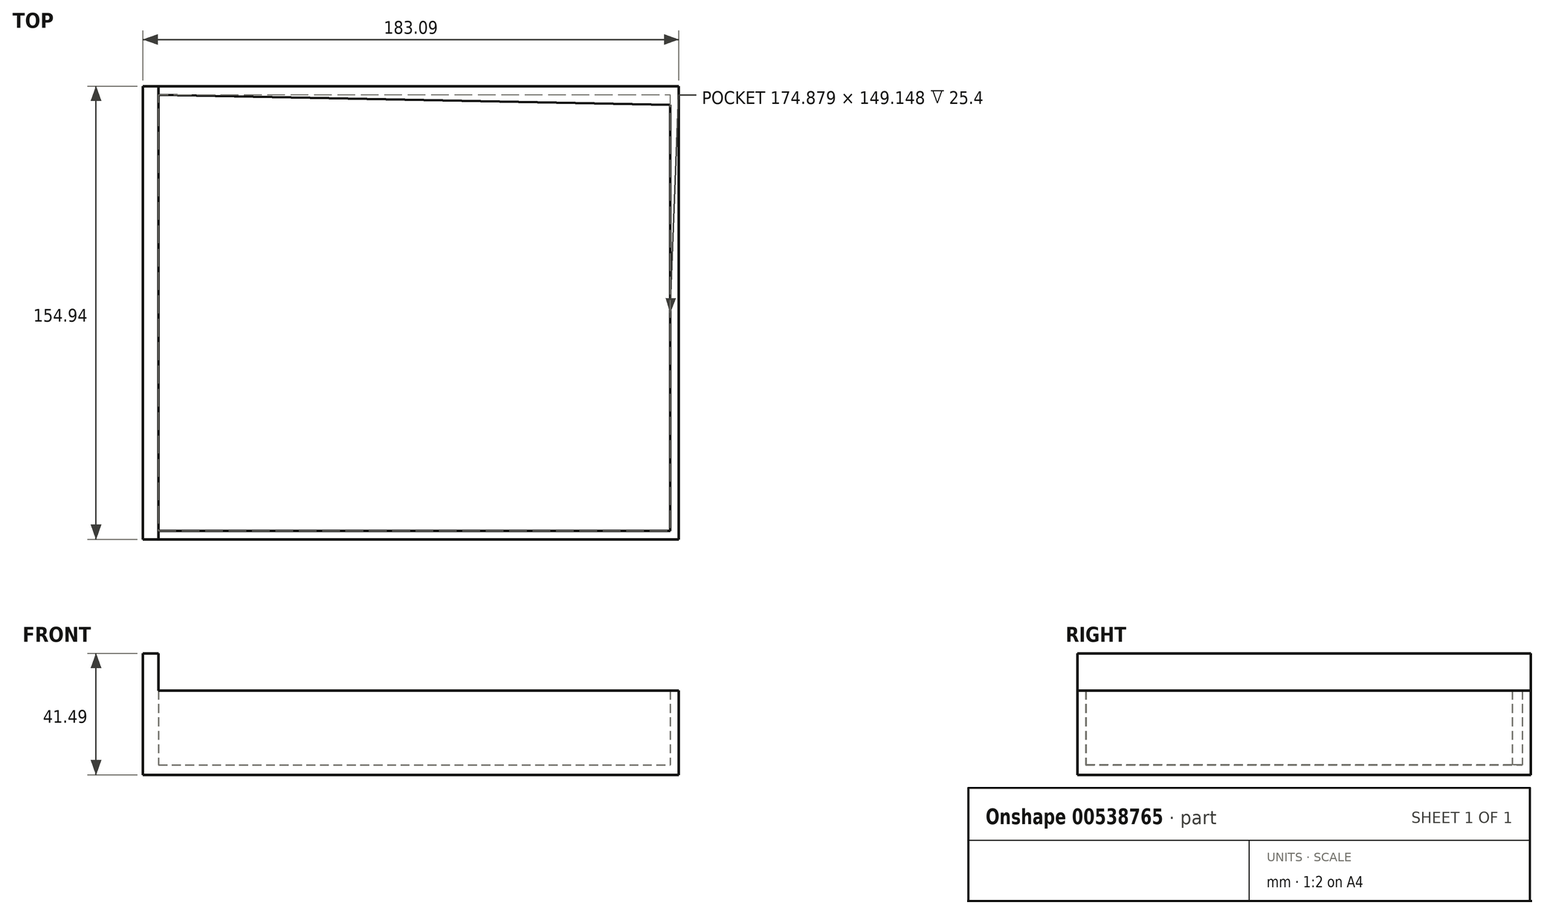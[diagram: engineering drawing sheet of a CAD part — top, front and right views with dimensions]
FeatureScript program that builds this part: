
annotation { "Feature Type Name" : "Feature", "Feature Type Description" : "" }
export const myFeature = defineFeature(function(context is Context, id is Id, definition is map)
    precondition{}
    {
        {
            var Q0;
            Q0=qCreatedBy(makeId("Front.planeOp"),FACE);
            var sketch = newSketch(context, id + "F0", { "sketchPlane" : qUnion([Q0])});
            skLineSegment(sketch, "E0.top", {"start": v(0, 38.1) * mm, "end": v(-5.29, 38.1) * mm});
            skLineSegment(sketch, "E0.left", {"start": v(0, 0) * mm, "end": v(0, 38.1) * mm});
            skLineSegment(sketch, "E1", {"start": v(0, 0) * mm, "end": v(177.8, 0) * mm});
            skLineSegment(sketch, "E2", {"start": v(177.8, 0) * mm, "end": v(177.8, -3.39) * mm});
            skLineSegment(sketch, "E3", {"start": v(177.8, -3.39) * mm, "end": v(-5.29, -3.39) * mm});
            skLineSegment(sketch, "E4", {"start": v(-5.29, 38.1) * mm, "end": v(-5.29, -3.39) * mm});
            skSolve(sketch);
        }
        {
            var Q0;
            Q0 = qSketchRegion(id + "F0", true);
            extrude(context, id + "F1", {"entities" : qUnion([Q0]), "endBound" : BoundingType.SYMMETRIC, "depth" : 154.94 * mm, "offsetDistance" : 25.4 * mm});
        }
        {
            var Q0;
            Q0=makeQuery(id+"F1.opExtrude","SWEPT_FACE",FACE,{"disambiguationData":[OSD([sQuery(id+"F0.wireOp",EDGE,"E0.left")])]});
            var sketch = newSketch(context, id + "F2", { "sketchPlane" : qUnion([Q0])});
            skLineSegment(sketch, "E5.bottom", {"start": v(-64.77, 55.88) * mm, "end": v(64.77, 55.88) * mm});
            skLineSegment(sketch, "E5.top", {"start": v(-64.77, 0) * mm, "end": v(64.77, 0) * mm});
            skLineSegment(sketch, "E5.left", {"start": v(-64.77, 55.88) * mm, "end": v(-64.77, 0) * mm});
            skLineSegment(sketch, "E5.right", {"start": v(64.77, 55.88) * mm, "end": v(64.77, 0) * mm});
            skSolve(sketch);
        }
        {
            var Q0;
            Q0=makeQuery(id+"FWv1kH76DlVqDbQ_1.boolean.opBoolean","MERGE",FACE,{"derivedFrom":[makeQuery(id+"F1.opExtrude","SWEPT_FACE",FACE,{"disambiguationData":[OSD([sQuery(id+"F0.wireOp",EDGE,"E1")])]}),makeQuery(id+"FWv1kH76DlVqDbQ_1.opExtrude","SWEPT_FACE",FACE,{"disambiguationData":[OSD([sQuery(id+"F2.wireOp",EDGE,"E5.top")])]})]});
            var sketch = newSketch(context, id + "F3", { "sketchPlane" : qUnion([Q0])});
            skLineSegment(sketch, "E6", {"start": v(0, -77.47) * mm, "end": v(177.8, -77.47) * mm});
            skLineSegment(sketch, "E7", {"start": v(177.8, -77.47) * mm, "end": v(177.8, 77.47) * mm});
            skLineSegment(sketch, "E8", {"start": v(177.8, 77.47) * mm, "end": v(0, 77.47) * mm});
            skLineSegment(sketch, "E9", {"start": v(0, 77.47) * mm, "end": v(-0.06, 74.55) * mm});
            skLineSegment(sketch, "E10", {"start": v(-0.06, 74.55) * mm, "end": v(174.88, 71.13) * mm});
            skLineSegment(sketch, "E11", {"start": v(174.88, 71.13) * mm, "end": v(174.88, -74.6) * mm});
            skLineSegment(sketch, "E12", {"start": v(174.88, -74.6) * mm, "end": v(0, -74.56) * mm});
            skLineSegment(sketch, "E13", {"start": v(0, -77.47) * mm, "end": v(0, -74.56) * mm});
            skSolve(sketch);
        }
        {
            var Q0;
            Q0 = qSketchRegion(id + "F3", true);
            extrude(context, id + "F4", {"entities" : qUnion([Q0]), "operationType" : NewBodyOperationType.ADD, "depth" : 25.4 * mm, "offsetDistance" : 25.4 * mm});
        }
    });
